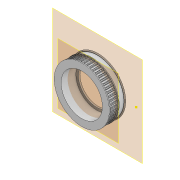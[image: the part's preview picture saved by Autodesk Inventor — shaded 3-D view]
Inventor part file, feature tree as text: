
AUTODESK INVENTOR PART (.ipt)
format: ipt  version: 2022 (Build 260153000, 153)  size: 654,336 bytes
history: native  units: mm
features: sketch x7, extrude x6, reference x5, plane x2, projected_geometry x2, other x2, fillet x1, pattern_circular x1, chamfer x1
ambient origin geometry x8: Origin, YZ Plane, XZ Plane, XY Plane, X Axis, Y Axis, Z Axis, Center Point
bodies: Volumenkörper1 (feature_tree)
feature tree (27):
  plane  "Arbeitsebene1"
  extrude  "Extrusion1"  Depth=9.0mm
  extrude  "Extrusion2"  Depth=8.0mm
  fillet  "Rundung1"  Radius=32.2mm
  pattern_circular  "Runde Anordnung1"  Count=52 Angle=360.0deg
  extrude  "Extrusion3"  Depth=0.5mm TaperAngle=0.0deg
  plane  "Arbeitsebene2"
  extrude  "Extrusion4"  [1 undecoded]
  extrude  "Extrusion5"  Depth=0.5mm TaperAngle=0.0deg
  sketch  "Skizze6"  dims[d11=5.0mm d12=0.0mm]
  extrude  "Extrusion6"  Depth=0.5mm TaperAngle=0.0deg
  chamfer  "Fase2"  Distance=1.5mm
  sketch  "Skizze1"  dims[d2=9.0mm d3=0.0mm d4=8.0mm]
  reference  "Referenz1"
  reference  "Referenz2"
  reference  "Referenz3"
  reference  "Referenz4"
  reference  "Referenz5"
  sketch  "Skizze2"  dims[d5=8.0mm d6=8.0mm d7=32.2mm]
  projected_geometry  "Projizierte Kontur1"
  sketch  "Skizze3"  dims[d8=25.15mm]
  sketch  "Skizze4"  dims[d9=1.0mm]
  projected_geometry  "Projizierte Kontur2"
  sketch  "Skizze5"  dims[d10=0.8mm]
  sketch  "Skizze7"  dims[d13=0.2mm d14=520.0mm d15=360.0deg d17=0.5mm d18=0.0mm d19=-4.0mm d20=0.5mm d21=0.0mm d22=0.5mm d23=0.0mm d27=1.5mm d28=1.0mm d29=0.0mm d30=0.5mm d31=2.0mm d32=45.0deg]
  other  "Assembly_Cube_Template_rotational_filtermount_v3.iam"
  other  "20_Cube_Insert_rotational_filtermount_v3.iam:1"
note: 1 required parameter value undecoded (feature->parameter linkage not recoverable at this tier; creation-order binding heuristic only, values carry confidence <= 0.55)
